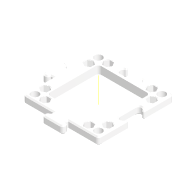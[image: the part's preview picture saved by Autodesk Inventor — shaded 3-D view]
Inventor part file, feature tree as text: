
AUTODESK INVENTOR PART (.ipt)
format: ipt  version: 2022 (Build 260153000, 153)  size: 634,880 bytes
history: native  units: mm
features: sketch x6, projected_geometry x5, extrude x3, hole x3, mirror x2, chamfer x2, other x1, pattern_circular x1, fillet x1
ambient origin geometry x8: Origin, YZ Plane, XZ Plane, XY Plane, X Axis, Y Axis, Z Axis, Center Point
bodies: Volumenkörper1 (feature_tree)
feature tree (24):
  extrude  "Extrusion1"  TaperAngle=0.0deg  [1 undecoded]
  mirror  "Mirror6"
  mirror  "Mirror7"
  extrude  "Extrusion13"  TaperAngle=0.0deg  [1 undecoded]
  extrude  "Extrusion14"  TaperAngle=0.0deg  [1 undecoded]
  other  "Work Axis4"
  pattern_circular  "Circular Pattern6"  [2 undecoded]
  hole  "Hole7"  [1 undecoded]
  chamfer  "Fase4"  [1 undecoded]
  fillet  "Rundung5"  Radius=3.0mm
  sketch  "Skizze36"  dims[d20=0.0mm]
  hole  "Bohrung8"  [1 undecoded]
  chamfer  "Fase6"  [1 undecoded]
  hole  "Bohrung9"  [1 undecoded]
  sketch  "Skizze1"  dims[d5=0.0mm d6=0.0mm]
  sketch  "Sketch26"  dims[d7=0.0mm d8=0.0mm]
  projected_geometry  "Projected Loop21"
  sketch  "Sketch28"  dims[d9=0.0mm d13=0.0mm]
  sketch  "Sketch29"  dims[d14=0.0mm]
  projected_geometry  "Projected Loop24"
  projected_geometry  "Projizierte Kontur27"
  projected_geometry  "Projizierte Kontur29"
  sketch  "Skizze37"  dims[d21=0.0mm d22=0.0mm d23=0.0mm d24=0.0mm d25=3.0mm d26=0.0mm d27=0.0mm d28=0.0mm d29=0.0mm d30=0.0mm d31=0.0mm d32=0.0mm d33=0.0mm d34=0.0mm d46=0.0mm d47=0.0mm d48=0.0mm d49=-10.0mm d50=0.0mm d51=0.0mm d52=0.0mm d53=0.0mm d54=0.0mm d55=0.0mm d56=0.0mm d57=0.0mm d58=0.0mm d59=0.0mm d77=2.65mm d82=2.65mm d222=0.5mm d236=5.3mm d278=25.0mm d279=25.0mm d2=8.0mm d281=8.0mm d282=2.0mm d286=5.1mm d290=20.8mm d292=2.0mm d293=5.6mm d298=10.0mm d299=0.0mm d300=2.0mm d301=0.25mm d302=10.0mm d303=0.0mm d308=20.0mm d309=90.0deg d313=6.3mm d314=6.3mm d319=7.78mm d320=5.0mm d322=5.0mm d323=3.2mm d324=6.0mm d325=7.0mm d326=3.0mm d327=90.0deg d328=8.0mm d329=20.594885mm d331=0.0mm d332=0.0mm d360=0.5mm d361=2.0mm d362=45.0deg d365=6.9mm d367=6.9mm d369=4.2mm d370=0.0mm d380=45.0deg d384=0.85mm d385=5.0mm d386=5.0mm d387=2.0mm d388=0.25mm d391=0.1mm d392=5.05mm d393=5.05mm d394=1.96mm d396=5.45mm d397=7.05mm d403=42.0mm d404=42.0mm d405=5.0mm d406=6.0mm d407=6.5mm d408=16.0mm d409=90.0deg d410=8.0mm d411=20.594885mm d415=0.75mm d416=2.0mm d417=45.0deg d418=6.0mm d419=6.0mm d420=3.5mm d421=6.0mm d422=90.0deg d423=0.1mm d424=0.0mm]
  projected_geometry  "Projizierte Kontur30"
note: 10 required parameter values undecoded (feature->parameter linkage not recoverable at this tier; creation-order binding heuristic only, values carry confidence <= 0.55)
